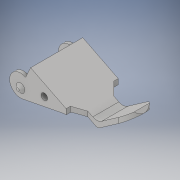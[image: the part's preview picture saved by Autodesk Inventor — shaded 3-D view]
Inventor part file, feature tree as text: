
AUTODESK INVENTOR PART (.ipt)
format: ipt  version: 2019 (Build 230136000, 136)  size: 175,104 bytes
history: native  units: mm
features: other x14, sketch x4, extrude x3, revolve x1
ambient origin geometry x8: Origin, YZ Plane, XZ Plane, XY Plane, X Axis, Y Axis, Z Axis, Center Point
bodies: Solid1 (feature_tree)
feature tree (22):
  extrude  "Extrusion1"  Depth=10.5mm TaperAngle=0.0deg
  extrude  "Extrusion2"  TaperAngle=360.0deg  [1 undecoded]
  extrude  "Extrusion3"  [1 undecoded]
  revolve  "Revolution1"  [1 undecoded]
  other  "A_XY"
  other  "A_YZ"
  other  "A_ZX"
  other  "A_X"
  other  "A_Y"
  other  "A_Z"
  other  "A_Center"
  other  "B_XY"
  other  "B_YZ"
  other  "B_ZX"
  other  "B_X"
  other  "B_Y"
  other  "B_Z"
  other  "B_Center"
  sketch  "Sketch_1"  dims[d0=12.0mm d1=0.0mm d2=10.5mm d3=0.0mm]
  sketch  "Sketch_2"  dims[d4=15.0mm d5=0.0mm d6=360.0deg]
  sketch  "Sketch_3"
  sketch  "Sketch_4"
note: 3 required parameter values undecoded (feature->parameter linkage not recoverable at this tier; creation-order binding heuristic only, values carry confidence <= 0.55)
